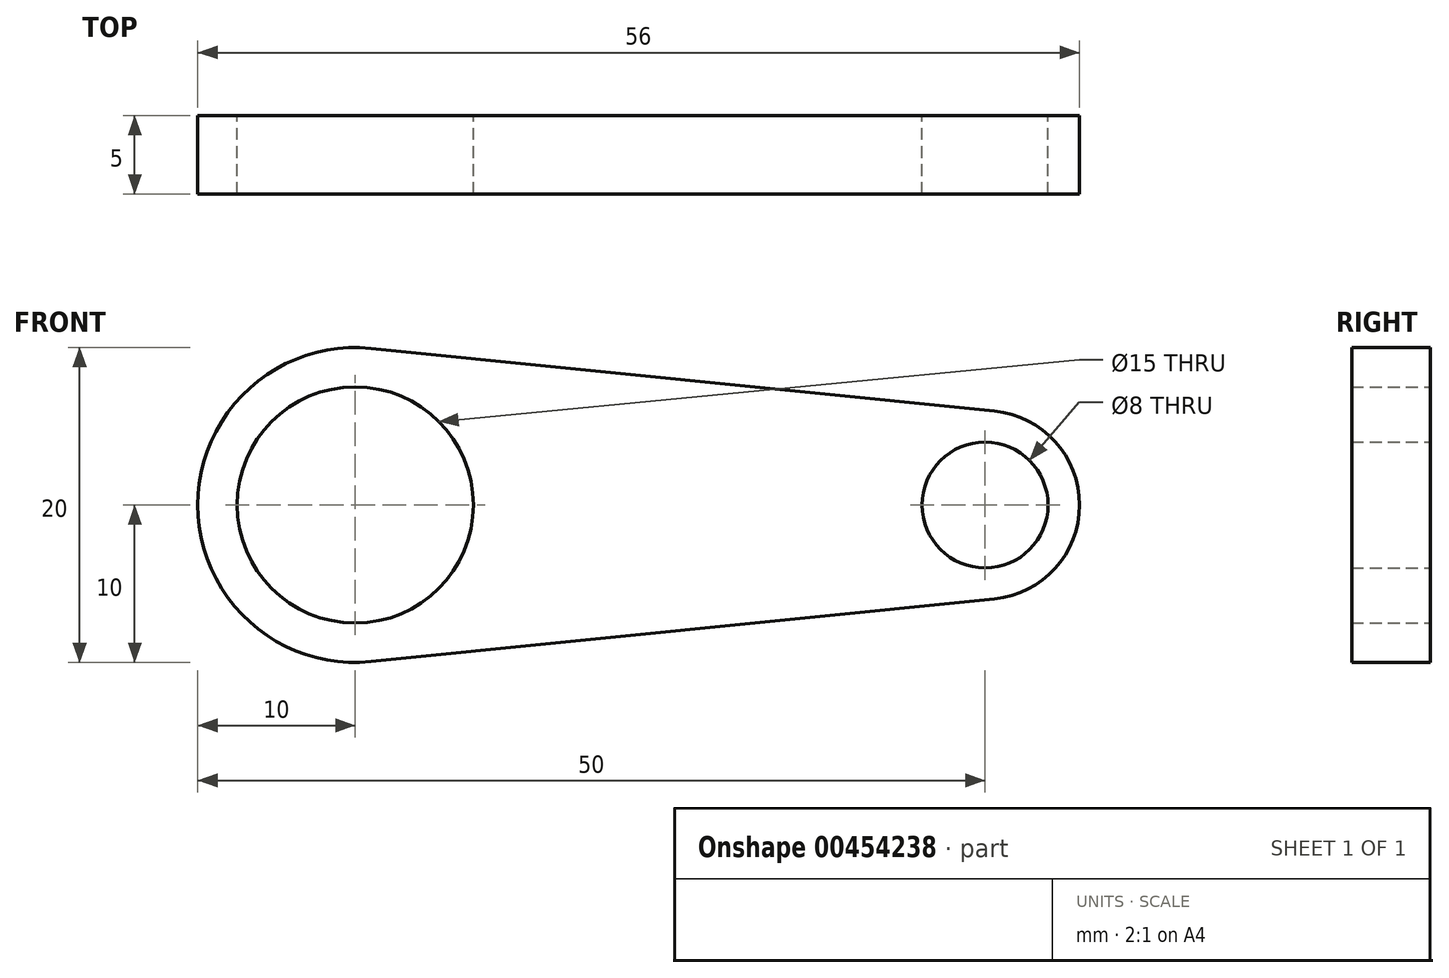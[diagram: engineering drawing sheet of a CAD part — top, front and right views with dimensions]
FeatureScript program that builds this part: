
annotation { "Feature Type Name" : "Feature", "Feature Type Description" : "" }
export const myFeature = defineFeature(function(context is Context, id is Id, definition is map)
    precondition{}
    {
        {
            var Q0;
            Q0=qCreatedBy(makeId("Front.planeOp"),FACE);
            var sketch = newSketch(context, id + "F0", { "sketchPlane" : qUnion([Q0])});
            skCircle(sketch, "E0", {"center": v(-40, 0) * mm, "radius": 7.5 * mm});
            skCircle(sketch, "E1", {"center": v(0, 0) * mm, "radius": 4 * mm});
            skArc(sketch, "E2.0", {"start": v(0.6, -5.97) * mm, "mid": v(6, 0) * mm, "end": v(0.6, 5.97) * mm});
            skArc(sketch, "E3.0", {"start": v(-39, 9.95) * mm, "mid": v(-50, 0) * mm, "end": v(-39, -9.95) * mm});
            skLineSegment(sketch, "E4", {"start": v(-39, 9.95) * mm, "end": v(0.6, 5.97) * mm});
            skLineSegment(sketch, "E5", {"start": v(-39, -9.95) * mm, "end": v(0.6, -5.97) * mm});
            skSolve(sketch);
        }
        {
            var Q0;
            Q0 = qSketchRegion(id + "F0", true);
            extrude(context, id + "F1", {"entities" : qUnion([Q0]), "depth" : 5 * mm});
        }
    });
